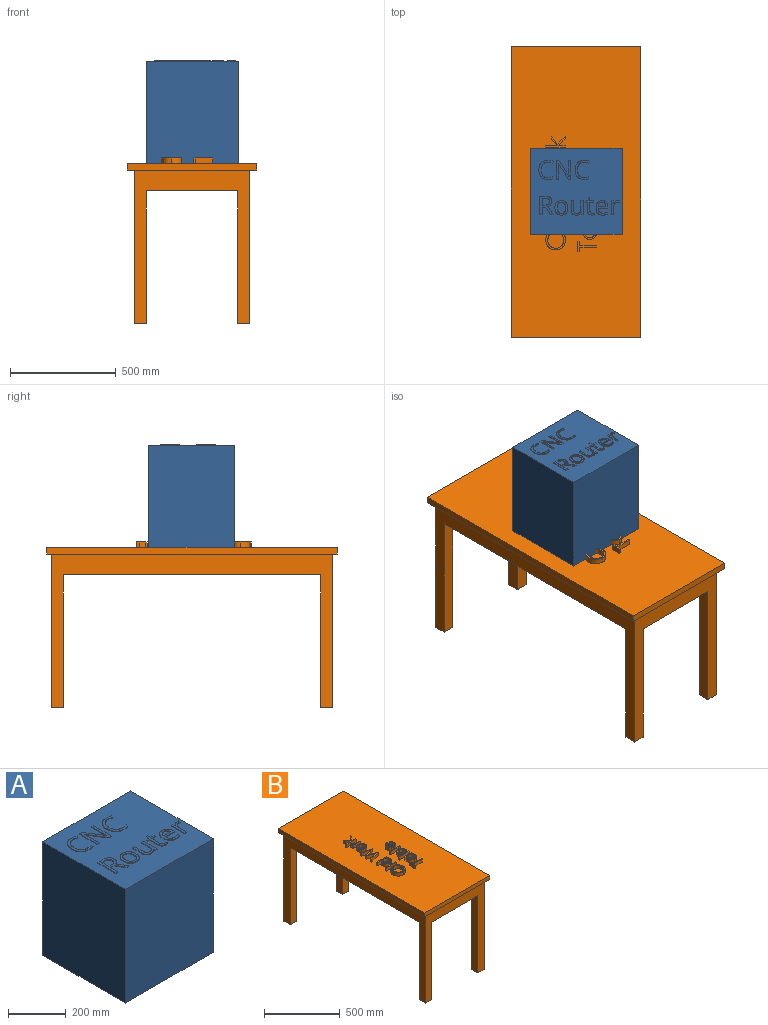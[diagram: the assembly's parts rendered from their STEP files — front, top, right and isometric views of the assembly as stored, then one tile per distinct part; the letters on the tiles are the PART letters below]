
ASSEMBLY  parts=2 mates=1
PART A: 166 faces, bbox 431.8x406.4x485.1 mm
  f0: plane 431.8x406.4mm, normal (0,0,1), area 156819.1mm2, adj f1,f2,f3,f4,f6,f7,f8,f9
  f1: plane 482.6x431.8mm, normal (0,1,0), area 208386.7mm2, adj f0,f2,f4,f5
  f2: plane 482.6x406.4mm, normal (-1,0,0), area 196128.6mm2, adj f0,f1,f3,f5
  f3: plane 482.6x431.8mm, normal (0,-1,0), area 208386.7mm2, adj f0,f2,f4,f5
  f4: plane 482.6x406.4mm, normal (1,0,0), area 196128.6mm2, adj f0,f1,f3,f5
  f5: plane 431.8x406.4mm, normal (0,0,-1), area 175483.5mm2, adj f1,f2,f3,f4
  f6: extruded ~22.94x9.68mm, area 65.3mm2, adj f0,f7,f20,f21
  f7: extruded ~20.03x4.69mm, area 52.7mm2, adj f0,f6,f8,f21
  f8: plane 8.8x4.34mm, normal (0.9,-0.44,0), area 24.9mm2, adj f0,f7,f9,f21
  f9: extruded ~24.23x5.05mm, area 63.4mm2, adj f0,f8,f10,f21
  f10: extruded ~22.64x5.55mm, area 59.9mm2, adj f0,f9,f11,f21
  f11: extruded ~15.79x14.71mm, area 55.6mm2, adj f0,f10,f12,f21
  f12: extruded ~23.87x5.09mm, area 62.5mm2, adj f0,f11,f13,f21
  f13: extruded ~33.59x10.58mm, area 91.5mm2, adj f0,f12,f14,f21
  f14: extruded ~30.05x11.83mm, area 84.6mm2, adj f0,f13,f15,f21
  f15: extruded ~22.61x3.45mm, area 58.4mm2, adj f0,f14,f16,f21
  f16: plane 8.97x2.54mm, normal (1,0,0), area 22.8mm2, adj f0,f15,f17,f21
  f17: extruded ~21.05x3.32mm, area 54.3mm2, adj f0,f16,f18,f21
  f18: extruded ~23.12x9.44mm, area 65.6mm2, adj f0,f17,f19,f21
  f19: extruded ~26.73x8.11mm, area 72.5mm2, adj f0,f18,f20,f21
  f20: extruded ~26.5x8.41mm, area 72.2mm2, adj f0,f6,f19,f21
  f21: plane 90.62x66.68mm, normal (0,0,1), area 1699.1mm2, adj f6,f7,f8,f9,f10,f11,f12,f13
  f22: plane 11.69x2.54mm, normal (0,-1,0), area 29.7mm2, adj f0,f23,f36,f37
  f23: plane 88.15x2.54mm, normal (1,0,0), area 223.9mm2, adj f0,f22,f24,f37
  f24: plane 9.59x2.54mm, normal (0,1,0), area 24.4mm2, adj f0,f23,f25,f37
  f25: plane 50.59x2.54mm, normal (-1,0,0), area 128.5mm2, adj f0,f24,f26,f37
  f26: extruded ~12.64x2.54mm, area 32.1mm2, adj f0,f25,f27,f37
  f27: extruded ~10.46x2.54mm, area 26.6mm2, adj f0,f26,f28,f37
  f28: plane 2.54x0.48mm, normal (0,1,0), area 1.2mm2, adj f0,f27,f29,f37
  f29: plane 73.68x48.06mm, normal (0.84,0.55,0), area 223.4mm2, adj f0,f28,f30,f37
  f30: plane 11.58x2.54mm, normal (0,1,0), area 29.4mm2, adj f0,f29,f31,f37
  f31: plane 88.15x2.54mm, normal (-1,0,0), area 223.9mm2, adj f0,f30,f32,f37
  f32: plane 9.47x2.54mm, normal (0,-1,0), area 24.1mm2, adj f0,f31,f33,f37
  f33: plane 50.1x2.54mm, normal (1,0,0), area 127.3mm2, adj f0,f32,f34,f37
  f34: extruded ~23.87x2.54mm, area 60.7mm2, adj f0,f33,f35,f37
  f35: plane 2.54x0.48mm, normal (0,-1,0), area 1.2mm2, adj f0,f34,f36,f37
  f36: plane 73.97x48.17mm, normal (-0.84,-0.55,0), area 224.2mm2, adj f0,f22,f35,f37
  f37: plane 88.15x68.86mm, normal (0,0,1), area 2565mm2, adj f22,f23,f24,f25,f26,f27,f28,f29
  f38: extruded ~22.94x9.68mm, area 65.3mm2, adj f0,f39,f52,f53
  f39: extruded ~20.03x4.69mm, area 52.7mm2, adj f0,f38,f40,f53
  f40: plane 8.8x4.34mm, normal (0.9,-0.44,0), area 24.9mm2, adj f0,f39,f41,f53
  f41: extruded ~24.23x5.05mm, area 63.4mm2, adj f0,f40,f42,f53
  f42: extruded ~22.64x5.55mm, area 59.9mm2, adj f0,f41,f43,f53
  f43: extruded ~15.79x14.71mm, area 55.6mm2, adj f0,f42,f44,f53
  f44: extruded ~23.87x5.09mm, area 62.5mm2, adj f0,f43,f45,f53
  f45: extruded ~33.59x10.58mm, area 91.5mm2, adj f0,f44,f46,f53
  f46: extruded ~30.05x11.83mm, area 84.6mm2, adj f0,f45,f47,f53
  f47: extruded ~22.61x3.45mm, area 58.4mm2, adj f0,f46,f48,f53
  f48: plane 8.97x2.54mm, normal (1,0,0), area 22.8mm2, adj f0,f47,f49,f53
  f49: extruded ~21.05x3.32mm, area 54.3mm2, adj f0,f48,f50,f53
  f50: extruded ~23.12x9.44mm, area 65.6mm2, adj f0,f49,f51,f53
  f51: extruded ~26.73x8.11mm, area 72.5mm2, adj f0,f50,f52,f53
  f52: extruded ~26.5x8.41mm, area 72.2mm2, adj f0,f38,f51,f53
  f53: plane 90.62x66.68mm, normal (0,0,1), area 1699.1mm2, adj f38,f39,f40,f41,f42,f43,f44,f45
  f54: plane 14.06x2.54mm, normal (0,1,0), area 35.7mm2, adj f55,f71,f72,f73
  f55: plane 33.7x2.54mm, normal (1,0,0), area 85.6mm2, adj f54,f56,f72,f73
  f56: plane 13.33x2.54mm, normal (0,-1,0), area 33.9mm2, adj f55,f57,f72,f73
  f57: extruded ~16.55x3.86mm, area 43.9mm2, adj f56,f58,f72,f73
  f58: extruded ~12.6x5.15mm, area 35.9mm2, adj f57,f59,f72,f73
  f59: extruded ~12.94x5.06mm, area 36.5mm2, adj f58,f71,f72,f73
  f60: plane 36.66x2.54mm, normal (1,0,0), area 93.1mm2, adj f0,f61,f70,f72
  f61: plane 18.41x2.54mm, normal (0,-1,0), area 46.7mm2, adj f0,f60,f62,f72
  f62: plane 36.66x21.34mm, normal (-0.86,-0.5,0), area 107.7mm2, adj f0,f61,f63,f72
  f63: plane 12.12x2.54mm, normal (0,-1,0), area 30.8mm2, adj f0,f62,f64,f72
  f64: plane 39.61x23.94mm, normal (0.86,0.52,0), area 117.6mm2, adj f0,f63,f65,f72
  f65: extruded ~23.63x17.73mm, area 80.9mm2, adj f0,f64,f66,f72
  f66: extruded ~18.69x7.75mm, area 53.3mm2, adj f0,f65,f67,f72
  f67: extruded ~23.97x6.21mm, area 64.1mm2, adj f0,f66,f68,f72
  f68: plane 24.17x2.54mm, normal (0,1,0), area 61.4mm2, adj f0,f67,f69,f72
  f69: plane 88.15x2.54mm, normal (-1,0,0), area 223.9mm2, adj f0,f68,f70,f72
  f70: plane 10.24x2.54mm, normal (0,-1,0), area 26mm2, adj f0,f60,f69,f72
  f71: extruded ~15.91x4.31mm, area 42.7mm2, adj f54,f59,f72,f73
  f72: plane 88.15x62.1mm, normal (0,0,1), area 2329.9mm2, adj f54,f55,f56,f57,f58,f59,f60,f61
  f73: plane 35.04x33.7mm, normal (0,0,1), area 1067.5mm2, adj f54,f55,f56,f57,f58,f59,f71
  f74: extruded ~19.3x5.06mm, area 51.6mm2, adj f75,f90,f91,f92
  f75: extruded ~19.23x5.01mm, area 51.4mm2, adj f74,f76,f91,f92
  f76: extruded ~14.83x6.45mm, area 42.6mm2, adj f75,f77,f91,f92
  f77: extruded ~15.05x6.54mm, area 43.3mm2, adj f76,f78,f91,f92
  f78: extruded ~19.14x5.09mm, area 51.2mm2, adj f77,f79,f91,f92
  f79: extruded ~19.33x5.09mm, area 51.7mm2, adj f78,f80,f91,f92
  f80: extruded ~14.93x6.6mm, area 43.1mm2, adj f79,f90,f91,f92
  f81: extruded ~25.24x8.13mm, area 68.9mm2, adj f0,f82,f89,f91
  f82: extruded ~24.96x8.17mm, area 68.2mm2, adj f0,f81,f83,f91
  f83: extruded ~22.02x9.23mm, area 62.6mm2, adj f0,f82,f84,f91
  f84: extruded ~22.44x9.02mm, area 63.4mm2, adj f0,f83,f85,f91
  f85: extruded ~25.17x8.08mm, area 68.7mm2, adj f0,f84,f86,f91
  f86: extruded ~18.21x3.74mm, area 47.6mm2, adj f0,f85,f87,f91
  f87: extruded ~11.94x10.61mm, area 41.2mm2, adj f0,f86,f88,f91
  f88: extruded ~15.74x4.17mm, area 41.9mm2, adj f0,f87,f89,f91
  f89: extruded ~22.49x9.08mm, area 63.6mm2, adj f0,f81,f88,f91
  f90: extruded ~14.88x6.63mm, area 43mm2, adj f74,f80,f91,f92
  f91: plane 68.51x60.71mm, normal (0,0,1), area 1677.1mm2, adj f74,f75,f76,f77,f78,f79,f80,f81
  f92: plane 51.61x39.97mm, normal (0,0,1), area 1711.5mm2, adj f74,f75,f76,f77,f78,f79,f80,f90
  f93: plane 42.87x2.54mm, normal (1,0,0), area 108.9mm2, adj f0,f94,f109,f110
  f94: plane 10.13x2.54mm, normal (0,1,0), area 25.7mm2, adj f0,f93,f95,f110
  f95: plane 43.23x2.54mm, normal (-1,0,0), area 109.8mm2, adj f0,f94,f96,f110
  f96: extruded ~18.33x5.99mm, area 50.3mm2, adj f0,f95,f97,f110
  f97: extruded ~18.05x5.73mm, area 49.3mm2, adj f0,f96,f98,f110
  f98: extruded ~12.46x2.6mm, area 32.6mm2, adj f0,f97,f99,f110
  f99: extruded ~8.53x7.48mm, area 29.2mm2, adj f0,f98,f100,f110
  f100: plane 2.54x0.54mm, normal (0,-1,0), area 1.4mm2, adj f0,f99,f101,f110
  f101: plane 8.86x2.54mm, normal (-0.99,-0.16,0), area 22.8mm2, adj f0,f100,f102,f110
  f102: plane 8.26x2.54mm, normal (0,-1,0), area 21mm2, adj f0,f101,f103,f110
  f103: plane 66.08x2.54mm, normal (1,0,0), area 167.8mm2, adj f0,f102,f104,f110
  f104: plane 10.01x2.54mm, normal (0,1,0), area 25.4mm2, adj f0,f103,f105,f110
  f105: plane 34.73x2.54mm, normal (-1,0,0), area 88.2mm2, adj f0,f104,f106,f110
  f106: extruded ~18.51x4.78mm, area 49.5mm2, adj f0,f105,f107,f110
  f107: extruded ~15.16x5.66mm, area 42.5mm2, adj f0,f106,f108,f110
  f108: extruded ~11.51x3.97mm, area 31.8mm2, adj f0,f107,f109,f110
  f109: extruded ~12.06x3.68mm, area 32.8mm2, adj f0,f93,f108,f110
  f110: plane 67.29x55.27mm, normal (0,0,1), area 1589.5mm2, adj f93,f94,f95,f96,f97,f98,f99,f100
  f111: extruded ~5.13x2.54mm, area 13.1mm2, adj f0,f112,f129,f130
  f112: extruded ~7.78x3.19mm, area 22mm2, adj f0,f111,f113,f130
  f113: extruded ~9.15x2.84mm, area 24.9mm2, adj f0,f112,f114,f130
  f114: plane 38.89x2.54mm, normal (1,0,0), area 98.8mm2, adj f0,f113,f115,f130
  f115: plane 19.18x2.54mm, normal (0,-1,0), area 48.7mm2, adj f0,f114,f116,f130
  f116: plane 7.78x2.54mm, normal (1,0,0), area 19.7mm2, adj f0,f115,f117,f130
  f117: plane 19.18x2.54mm, normal (0,1,0), area 48.7mm2, adj f0,f116,f118,f130
  f118: plane 15.32x2.54mm, normal (1,0,0), area 38.9mm2, adj f0,f117,f119,f130
  f119: plane 5.79x2.54mm, normal (0,1,0), area 14.7mm2, adj f0,f118,f120,f130
  f120: plane 14.1x4.21mm, normal (-0.96,0.29,0), area 37.4mm2, adj f0,f119,f121,f130
  f121: plane 9.47x4.17mm, normal (-0.4,0.92,0), area 26.3mm2, adj f0,f120,f122,f130
  f122: plane 4.82x2.54mm, normal (-1,0,0), area 12.3mm2, adj f0,f121,f123,f130
  f123: plane 9.47x2.54mm, normal (0,-1,0), area 24.1mm2, adj f0,f122,f124,f130
  f124: plane 39.32x2.54mm, normal (-1,0,0), area 99.9mm2, adj f0,f123,f125,f130
  f125: extruded ~20.2x19.16mm, area 81.1mm2, adj f0,f124,f126,f130
  f126: extruded ~5.71x2.54mm, area 14.6mm2, adj f0,f125,f127,f130
  f127: extruded ~4.78x2.54mm, area 12.6mm2, adj f0,f126,f128,f130
  f128: plane 7.66x2.54mm, normal (1,0,0), area 19.5mm2, adj f0,f127,f129,f130
  f129: extruded ~3.92x2.54mm, area 10.2mm2, adj f0,f111,f128,f130
  f130: plane 82.61x39.13mm, normal (0,0,1), area 1129.7mm2, adj f111,f112,f113,f114,f115,f116,f117,f118
  f131: extruded ~12.69x5.18mm, area 35.9mm2, adj f132,f149,f150,f151
  f132: extruded ~12.07x5.04mm, area 34.4mm2, adj f131,f133,f150,f151
  f133: extruded ~14.49x4.22mm, area 39.1mm2, adj f132,f134,f150,f151
  f134: plane 34.55x2.54mm, normal (0,1,0), area 87.8mm2, adj f133,f149,f150,f151
  f135: extruded ~23.12x8.93mm, area 64.8mm2, adj f0,f136,f148,f150
  f136: extruded ~11.42x2.54mm, area 29.2mm2, adj f0,f135,f137,f150
  f137: extruded ~10.03x3.28mm, area 26.9mm2, adj f0,f136,f138,f150
  f138: plane 8.93x2.54mm, normal (1,0,0), area 22.7mm2, adj f0,f137,f139,f150
  f139: extruded ~21.09x4.46mm, area 55.1mm2, adj f0,f138,f140,f150
  f140: extruded ~15.7x6.03mm, area 44mm2, adj f0,f139,f141,f150
  f141: extruded ~17.66x5.88mm, area 48.3mm2, adj f0,f140,f142,f150
  f142: plane 45.51x2.54mm, normal (0,-1,0), area 115.6mm2, adj f0,f141,f143,f150
  f143: plane 6.33x2.54mm, normal (1,0,0), area 16.1mm2, adj f0,f142,f144,f150
  f144: extruded ~21.56x7.23mm, area 59.1mm2, adj f0,f143,f145,f150
  f145: extruded ~19.64x8.17mm, area 55.8mm2, adj f0,f144,f146,f150
  f146: extruded ~21.14x9.41mm, area 60.8mm2, adj f0,f145,f147,f150
  f147: extruded ~25.4x7.87mm, area 69mm2, adj f0,f146,f148,f150
  f148: extruded ~24.77x8.48mm, area 68.2mm2, adj f0,f135,f147,f150
  f149: extruded ~14.34x5.59mm, area 39.8mm2, adj f131,f134,f150,f151
  f150: plane 68.51x55.89mm, normal (0,0,1), area 1741.7mm2, adj f131,f132,f133,f134,f135,f136,f137,f138
  f151: plane 34.55x19.52mm, normal (0,0,1), area 543.8mm2, adj f131,f132,f133,f134,f149
  f152: extruded ~7.89x2.54mm, area 20.2mm2, adj f0,f153,f164,f165
  f153: extruded ~11.4x3.5mm, area 30.8mm2, adj f0,f152,f154,f165
  f154: extruded ~9.95x8.86mm, area 34.1mm2, adj f0,f153,f155,f165
  f155: plane 2.54x0.48mm, normal (0,1,0), area 1.2mm2, adj f0,f154,f156,f165
  f156: plane 12.23x2.54mm, normal (1,0.09,0), area 31.2mm2, adj f0,f155,f157,f165
  f157: plane 8.26x2.54mm, normal (0,1,0), area 21mm2, adj f0,f156,f158,f165
  f158: plane 66.08x2.54mm, normal (-1,0,0), area 167.8mm2, adj f0,f157,f159,f165
  f159: plane 10.01x2.54mm, normal (0,-1,0), area 25.4mm2, adj f0,f158,f160,f165
  f160: plane 35.46x2.54mm, normal (1,0,0), area 90.1mm2, adj f0,f159,f161,f165
  f161: extruded ~16.22x5.69mm, area 44.6mm2, adj f0,f160,f162,f165
  f162: extruded ~13.72x6.51mm, area 39.9mm2, adj f0,f161,f163,f165
  f163: extruded ~7.23x2.54mm, area 18.6mm2, adj f0,f162,f164,f165
  f164: plane 9.28x2.54mm, normal (0.99,-0.15,0), area 23.8mm2, adj f0,f152,f163,f165
  f165: plane 67.29x38.05mm, normal (0,0,1), area 910.5mm2, adj f152,f153,f154,f155,f156,f157,f158,f159
PART B: 163 faces, bbox 609.9x1371.7x781.1 mm
  f0: plane 1371.73x609.89mm, normal (0,0,1), area 803903mm2, adj f10,f11,f12,f13,f24,f25,f26,f27
  f1: plane 1371.73x609.89mm, normal (0,0,-1), area 111370.7mm2, adj f10,f11,f12,f13,f14,f15,f17,f19
  f2: plane 625.48x57.15mm, normal (-1,0,0), area 35745.9mm2, adj f3,f14,f16,f22
  f3: plane 625.48x57.15mm, normal (0,1,0), area 35745.9mm2, adj f2,f15,f16,f22
  f4: plane 625.48x57.15mm, normal (0,1,0), area 35745.9mm2, adj f5,f17,f18,f22
  f5: plane 625.48x57.15mm, normal (1,0,0), area 35745.9mm2, adj f4,f14,f18,f22
  f6: plane 625.48x57.15mm, normal (1,0,0), area 35745.9mm2, adj f7,f19,f20,f22
  f7: plane 625.48x57.15mm, normal (0,-1,0), area 35745.9mm2, adj f6,f17,f20,f22
  f8: plane 625.48x57.15mm, normal (0,-1,0), area 35745.9mm2, adj f9,f15,f21,f22
  f9: plane 625.48x57.15mm, normal (-1,0,0), area 35745.9mm2, adj f8,f19,f21,f22
  f10: plane 609.6x31.75mm, normal (0,-1,0), area 19354.8mm2, adj f0,f1,f11,f13
  f11: plane 1371.6x31.75mm, normal (1,0,0), area 43548.3mm2, adj f0,f1,f10,f12
  f12: plane 609.6x31.75mm, normal (0,1,0), area 19354.8mm2, adj f0,f1,f11,f13
  f13: plane 1371.6x31.75mm, normal (-1,0,0), area 43548.3mm2, adj f0,f1,f10,f12
  f14: plane 723.9x546.1mm, normal (0,-1,0), area 125241.7mm2, adj f1,f2,f5,f15,f16,f17,f18,f22
  f15: plane 1327.15x723.9mm, normal (1,0,0), area 202116.5mm2, adj f1,f3,f8,f14,f16,f19,f21,f22
  f16: plane 57.16x57.16mm, normal (0,0,-1), area 3266.1mm2, adj f2,f3,f14,f15
  f17: plane 1327.15x723.9mm, normal (-1,0,0), area 202116.5mm2, adj f1,f4,f7,f14,f18,f19,f20,f22
  f18: plane 57.16x57.16mm, normal (0,0,-1), area 3266.1mm2, adj f4,f5,f14,f17
  f19: plane 723.9x546.1mm, normal (0,1,0), area 125241.7mm2, adj f1,f6,f9,f15,f17,f20,f21,f22
  f20: plane 57.16x57.16mm, normal (0,0,-1), area 3266.1mm2, adj f6,f7,f17,f19
  f21: plane 57.16x57.16mm, normal (0,0,-1), area 3266.1mm2, adj f8,f9,f15,f19
  f22: plane 1327.24x546.36mm, normal (0,0,-1), area 711692.1mm2, adj f2,f3,f4,f5,f6,f7,f8,f9
  f23: plane 93.46x93.46mm, normal (0,0,1), area 2301.1mm2, adj f24,f25,f26,f27,f28,f29,f30,f31
  f24: extruded ~47.13x46.15mm, area 1864.4mm2, adj f0,f23,f25,f27
  f25: extruded ~46.88x46.33mm, area 1865mm2, adj f0,f23,f24,f26
  f26: extruded ~46.78x46.58mm, area 1868mm2, adj f0,f23,f25,f27
  f27: extruded ~47.31x46.68mm, area 1884.7mm2, adj f0,f23,f24,f26
  f28: extruded ~38.94x37.55mm, area 1529.2mm2, adj f23,f29,f31,f32
  f29: extruded ~38.57x37.98mm, area 1529.4mm2, adj f23,f28,f30,f32
  f30: extruded ~38.58x37.25mm, area 1516.9mm2, adj f23,f29,f31,f32
  f31: extruded ~38.92x37.67mm, area 1535.2mm2, adj f23,f28,f30,f32
  f32: plane 77.5x75.22mm, normal (0,0,1), area 4603.4mm2, adj f28,f29,f30,f31
  f33: plane 91.18x25.4mm, normal (0,-1,0), area 2316mm2, adj f0,f34,f36,f37
  f34: plane 25.4x7.98mm, normal (1,0,0), area 202.6mm2, adj f0,f33,f35,f37
  f35: plane 91.18x25.4mm, normal (0,1,0), area 2316mm2, adj f0,f34,f36,f37
  f36: plane 25.4x7.98mm, normal (-1,0,0), area 202.6mm2, adj f0,f33,f35,f37
  f37: plane 91.18x8mm, normal (0,0,1), area 727.4mm2, adj f33,f34,f35,f36
  f38: plane 92.33x68.39mm, normal (0,0,1), area 1979.8mm2, adj f39,f40,f41,f42,f43,f44,f45,f46
  f39: plane 25.4x7.98mm, normal (-1,0,0), area 202.6mm2, adj f0,f38,f40,f47
  f40: plane 38.79x25.4mm, normal (0,-1,0), area 985.2mm2, adj f0,f38,f39,f41
  f41: extruded ~26.29x25.4mm, area 784.2mm2, adj f0,f38,f40,f42
  f42: extruded ~34.11x33.45mm, area 1349.6mm2, adj f0,f38,f41,f43
  f43: extruded ~33.88x33.79mm, area 1353mm2, adj f0,f38,f42,f44
  f44: extruded ~26.53x25.4mm, area 770.2mm2, adj f0,f38,f43,f45
  f45: plane 25.4x11.24mm, normal (0,-1,0), area 285.4mm2, adj f0,f38,f44,f46
  f46: plane 25.4x7.98mm, normal (1,0,0), area 202.6mm2, adj f0,f38,f45,f47
  f47: plane 91.18x25.4mm, normal (0,1,0), area 2316mm2, adj f0,f38,f39,f46
  f48: extruded ~26.18x25.78mm, area 1042.2mm2, adj f38,f49,f51,f52
  f49: extruded ~26.24x25.56mm, area 1034.5mm2, adj f38,f48,f50,f52
  f50: extruded ~26.18x25.73mm, area 1034.4mm2, adj f38,f49,f51,f52
  f51: extruded ~26.24x25.51mm, area 1037.5mm2, adj f38,f48,f50,f52
  f52: plane 52.43x51.29mm, normal (0,0,1), area 2122.1mm2, adj f48,f49,f50,f51
  f53: plane 88.9x25.4mm, normal (0.26,-0.97,0), area 2336.6mm2, adj f0,f54,f65,f66
  f54: plane 25.4x1.14mm, normal (1,0,0), area 28.9mm2, adj f0,f53,f55,f66
  f55: plane 68x27.05mm, normal (0.37,0.93,0), area 1858.8mm2, adj f0,f54,f56,f66
  f56: plane 67.99x26.76mm, normal (0.37,-0.93,0), area 1855.9mm2, adj f0,f55,f57,f66
  f57: plane 25.4x1.14mm, normal (1,0,0), area 28.9mm2, adj f0,f56,f58,f66
  f58: plane 88.91x25.4mm, normal (0.26,0.97,0), area 2338.7mm2, adj f0,f57,f59,f66
  f59: plane 25.4x8.16mm, normal (-1,0,0), area 207.2mm2, adj f0,f58,f60,f66
  f60: plane 64.76x25.4mm, normal (-0.26,-0.97,0), area 1703.6mm2, adj f0,f59,f61,f66
  f61: plane 64.75x25.41mm, normal (-0.37,0.93,0), area 1766.7mm2, adj f0,f60,f62,f66
  f62: plane 25.4x1.16mm, normal (-1,0,0), area 29.4mm2, adj f0,f61,f63,f66
  f63: plane 65.2x25.86mm, normal (-0.37,-0.93,0), area 1781.7mm2, adj f0,f62,f64,f66
  f64: plane 65.19x25.4mm, normal (-0.26,0.97,0), area 1714mm2, adj f0,f63,f65,f66
  f65: plane 25.4x8.25mm, normal (-1,0,0), area 209.4mm2, adj f0,f53,f64,f66
  f66: plane 103.72x88.92mm, normal (0,0,1), area 2475.1mm2, adj f53,f54,f55,f56,f57,f58,f59,f60
  f67: plane 67.25x67.25mm, normal (0,0,1), area 1502.1mm2, adj f68,f69,f70,f71,f72,f73,f74,f75
  f68: extruded ~25.4x24.75mm, area 707.2mm2, adj f0,f67,f69,f73
  f69: extruded ~25.4x23.05mm, area 642.9mm2, adj f0,f67,f68,f70
  f70: extruded ~33.67x33.44mm, area 1344.2mm2, adj f0,f67,f69,f71
  f71: extruded ~33.58x33.45mm, area 1342.5mm2, adj f0,f67,f70,f72
  f72: extruded ~25.4x23.1mm, area 644.2mm2, adj f0,f67,f71,f73
  f73: extruded ~25.4x24.69mm, area 704.8mm2, adj f0,f67,f68,f72
  f74: extruded ~25.87x25.65mm, area 1028.6mm2, adj f67,f75,f77,f78
  f75: extruded ~25.88x25.64mm, area 1028.9mm2, adj f67,f74,f76,f78
  f76: extruded ~25.65x25.41mm, area 1022.3mm2, adj f67,f75,f77,f78
  f77: extruded ~25.64x25.42mm, area 1022.2mm2, adj f67,f74,f76,f78
  f78: plane 51.29x51.29mm, normal (0,0,1), area 2075.1mm2, adj f74,f75,f76,f77
  f79: plane 64.97x25.4mm, normal (0,-1,0), area 1650.1mm2, adj f0,f80,f89,f90
  f80: plane 25.4x7.98mm, normal (1,0,0), area 202.6mm2, adj f0,f79,f81,f90
  f81: plane 25.4x21.83mm, normal (0,1,0), area 554.6mm2, adj f0,f80,f82,f90
  f82: extruded ~25.4x22.3mm, area 568.5mm2, adj f0,f81,f83,f90
  f83: extruded ~25.4x14mm, area 519.5mm2, adj f0,f82,f84,f90
  f84: extruded ~25.4x4.08mm, area 108.5mm2, adj f0,f83,f85,f90
  f85: plane 25.4x6.91mm, normal (0.54,0.84,0), area 207.8mm2, adj f0,f84,f86,f90
  f86: extruded ~25.4x6.95mm, area 187.5mm2, adj f0,f85,f87,f90
  f87: extruded ~25.4x15.85mm, area 508.3mm2, adj f0,f86,f88,f90
  f88: plane 25.4x9.56mm, normal (0,1,0), area 242.9mm2, adj f0,f87,f89,f90
  f89: plane 25.4x7.98mm, normal (-1,0,0), area 202.6mm2, adj f0,f79,f88,f90
  f90: plane 66.11x30.77mm, normal (0,0,1), area 711.5mm2, adj f79,f80,f81,f82,f83,f84,f85,f86
  f91: plane 91.18x25.4mm, normal (0,-1,0), area 2316mm2, adj f0,f92,f101,f102
  f92: plane 25.4x7.98mm, normal (1,0,0), area 202.6mm2, adj f0,f91,f93,f102
  f93: plane 29.94x25.4mm, normal (0,1,0), area 760.4mm2, adj f0,f92,f94,f102
  f94: plane 33.01x29.93mm, normal (0.74,-0.67,0), area 1131.7mm2, adj f0,f93,f95,f102
  f95: plane 25.4x11.45mm, normal (1,0,0), area 290.9mm2, adj f0,f94,f96,f102
  f96: plane 37.73x34.18mm, normal (-0.74,0.67,0), area 1293.1mm2, adj f0,f95,f97,f102
  f97: plane 34.29x30.78mm, normal (0.74,0.67,0), area 1170.4mm2, adj f0,f96,f98,f102
  f98: plane 25.4x11.47mm, normal (-1,0,0), area 291.3mm2, adj f0,f97,f99,f102
  f99: plane 29.56x26.51mm, normal (-0.74,-0.67,0), area 1008.4mm2, adj f0,f98,f100,f102
  f100: plane 52.71x25.4mm, normal (0,1,0), area 1338.9mm2, adj f0,f99,f101,f102
  f101: plane 25.4x7.98mm, normal (-1,0,0), area 202.6mm2, adj f0,f91,f100,f102
  f102: plane 91.18x52.45mm, normal (0,0,1), area 1451.7mm2, adj f91,f92,f93,f94,f95,f96,f97,f98
  f103: plane 25.4x19.38mm, normal (1,0,0), area 492.1mm2, adj f0,f104,f110,f111
  f104: plane 79.78x25.4mm, normal (0,-1,0), area 2026.5mm2, adj f0,f103,f105,f111
  f105: plane 25.4x7.98mm, normal (1,0,0), area 202.6mm2, adj f0,f104,f106,f111
  f106: plane 79.78x25.4mm, normal (0,1,0), area 2026.5mm2, adj f0,f105,f107,f111
  f107: plane 25.4x19.38mm, normal (1,0,0), area 492.1mm2, adj f0,f106,f108,f111
  f108: plane 25.4x9.12mm, normal (0,1,0), area 231.6mm2, adj f0,f107,f109,f111
  f109: plane 46.73x25.4mm, normal (-1,0,0), area 1186.9mm2, adj f0,f108,f110,f111
  f110: plane 25.4x9.12mm, normal (0,-1,0), area 231.6mm2, adj f0,f103,f109,f111
  f111: plane 88.91x46.73mm, normal (0,0,1), area 1062.6mm2, adj f103,f104,f105,f106,f107,f108,f109,f110
  f112: plane 68.39x67.25mm, normal (0,0,1), area 1777.4mm2, adj f113,f114,f115,f116,f117,f118,f119,f120
  f113: plane 25.4x7.98mm, normal (-1,0,0), area 202.6mm2, adj f0,f112,f114,f121
  f114: plane 25.4x12.02mm, normal (0,-1,0), area 305.3mm2, adj f0,f112,f113,f115
  f115: extruded ~26.29x25.4mm, area 778.1mm2, adj f0,f112,f114,f116
  f116: extruded ~34.11x33.45mm, area 1349.6mm2, adj f0,f112,f115,f117
  f117: extruded ~33.88x33.79mm, area 1353mm2, adj f0,f112,f116,f118
  f118: extruded ~26.53x25.4mm, area 770.2mm2, adj f0,f112,f117,f119
  f119: plane 25.4x11.24mm, normal (0,-1,0), area 285.4mm2, adj f0,f112,f118,f120
  f120: plane 25.4x7.98mm, normal (1,0,0), area 202.6mm2, adj f0,f112,f119,f121
  f121: plane 64.97x25.4mm, normal (0,1,0), area 1650.1mm2, adj f0,f112,f113,f120
  f122: extruded ~26.18x25.78mm, area 1042.2mm2, adj f112,f123,f125,f126
  f123: extruded ~26.24x25.56mm, area 1034.5mm2, adj f112,f122,f124,f126
  f124: extruded ~26.18x25.73mm, area 1034.4mm2, adj f112,f123,f125,f126
  f125: extruded ~26.24x25.51mm, area 1037.5mm2, adj f112,f122,f124,f126
  f126: plane 52.43x51.29mm, normal (0,0,1), area 2122.1mm2, adj f122,f123,f124,f125
  f127: plane 92.31x68.4mm, normal (0,0,1), area 1980.4mm2, adj f128,f129,f130,f131,f132,f133,f134,f135
  f128: plane 25.4x7.98mm, normal (1,0,0), area 202.6mm2, adj f0,f127,f129,f136
  f129: plane 25.4x12.02mm, normal (0,1,0), area 305.3mm2, adj f0,f127,f128,f130
  f130: extruded ~26.25x25.4mm, area 776.9mm2, adj f0,f127,f129,f131
  f131: extruded ~34.15x33.51mm, area 1351.6mm2, adj f0,f127,f130,f132
  f132: extruded ~33.91x33.74mm, area 1352.4mm2, adj f0,f127,f131,f133
  f133: extruded ~26.5x25.4mm, area 775.8mm2, adj f0,f127,f132,f134
  f134: plane 38x25.4mm, normal (0,1,0), area 965.3mm2, adj f0,f127,f133,f135
  f135: plane 25.4x7.98mm, normal (-1,0,0), area 202.6mm2, adj f0,f127,f134,f136
  f136: plane 91.18x25.4mm, normal (0,-1,0), area 2316mm2, adj f0,f127,f128,f135
  f137: extruded ~26.18x25.76mm, area 1042mm2, adj f127,f138,f140,f141
  f138: extruded ~26.24x25.53mm, area 1033.6mm2, adj f127,f137,f139,f141
  f139: extruded ~26.13x25.76mm, area 1033.9mm2, adj f127,f138,f140,f141
  f140: extruded ~26.3x25.53mm, area 1038.3mm2, adj f127,f137,f139,f141
  f141: plane 52.43x51.29mm, normal (0,0,1), area 2121.3mm2, adj f137,f138,f139,f140
  f142: plane 91.18x25.4mm, normal (0,-1,0), area 2316mm2, adj f0,f143,f145,f146
  f143: plane 25.4x7.98mm, normal (1,0,0), area 202.6mm2, adj f0,f142,f144,f146
  f144: plane 91.18x25.4mm, normal (0,1,0), area 2316mm2, adj f0,f143,f145,f146
  f145: plane 25.4x7.98mm, normal (-1,0,0), area 202.6mm2, adj f0,f142,f144,f146
  f146: plane 91.18x8mm, normal (0,0,1), area 727.4mm2, adj f142,f143,f144,f145
  f147: plane 67.25x66.11mm, normal (0,0,1), area 1764.3mm2, adj f148,f149,f150,f151,f152,f153,f154,f155
  f148: extruded ~25.4x23.91mm, area 734.6mm2, adj f0,f147,f149,f157
  f149: extruded ~25.4x23.93mm, area 954.7mm2, adj f0,f147,f148,f150
  f150: plane 58.13x25.4mm, normal (1,0,0), area 1476.4mm2, adj f0,f147,f149,f151
  f151: extruded ~25.4x22.54mm, area 611.1mm2, adj f0,f147,f150,f152
  f152: extruded ~26.16x25.4mm, area 768.7mm2, adj f0,f147,f151,f153
  f153: extruded ~25.4x25.39mm, area 741.9mm2, adj f0,f147,f152,f154
  f154: extruded ~25.4x21.69mm, area 594.2mm2, adj f0,f147,f153,f155
  f155: extruded ~33.44x32.69mm, area 1328.8mm2, adj f0,f147,f154,f156
  f156: extruded ~30x25.4mm, area 938.4mm2, adj f0,f147,f155,f157
  f157: plane 25.4x7.09mm, normal (-0.89,0.46,0), area 203.3mm2, adj f0,f147,f148,f156
  f158: plane 49.31x25.4mm, normal (-1,0,0), area 1252.5mm2, adj f147,f159,f161,f162
  f159: extruded ~25.4x24.85mm, area 868.8mm2, adj f147,f158,f160,f162
  f160: extruded ~25.4x16.74mm, area 462.8mm2, adj f147,f159,f161,f162
  f161: extruded ~25.4x13.29mm, area 395.8mm2, adj f147,f158,f160,f162
  f162: plane 49.31x19.38mm, normal (0,0,1), area 719.5mm2, adj f158,f159,f160,f161
PLACE A t=(715.49,537.89,449.55)mm
PLACE B t=(-188.5,1165.04,2007.07)mm
MATE fastened A.f5 <-> B.f0  axis (0,0,-1) through (721.73,537.89,449.55)mm
